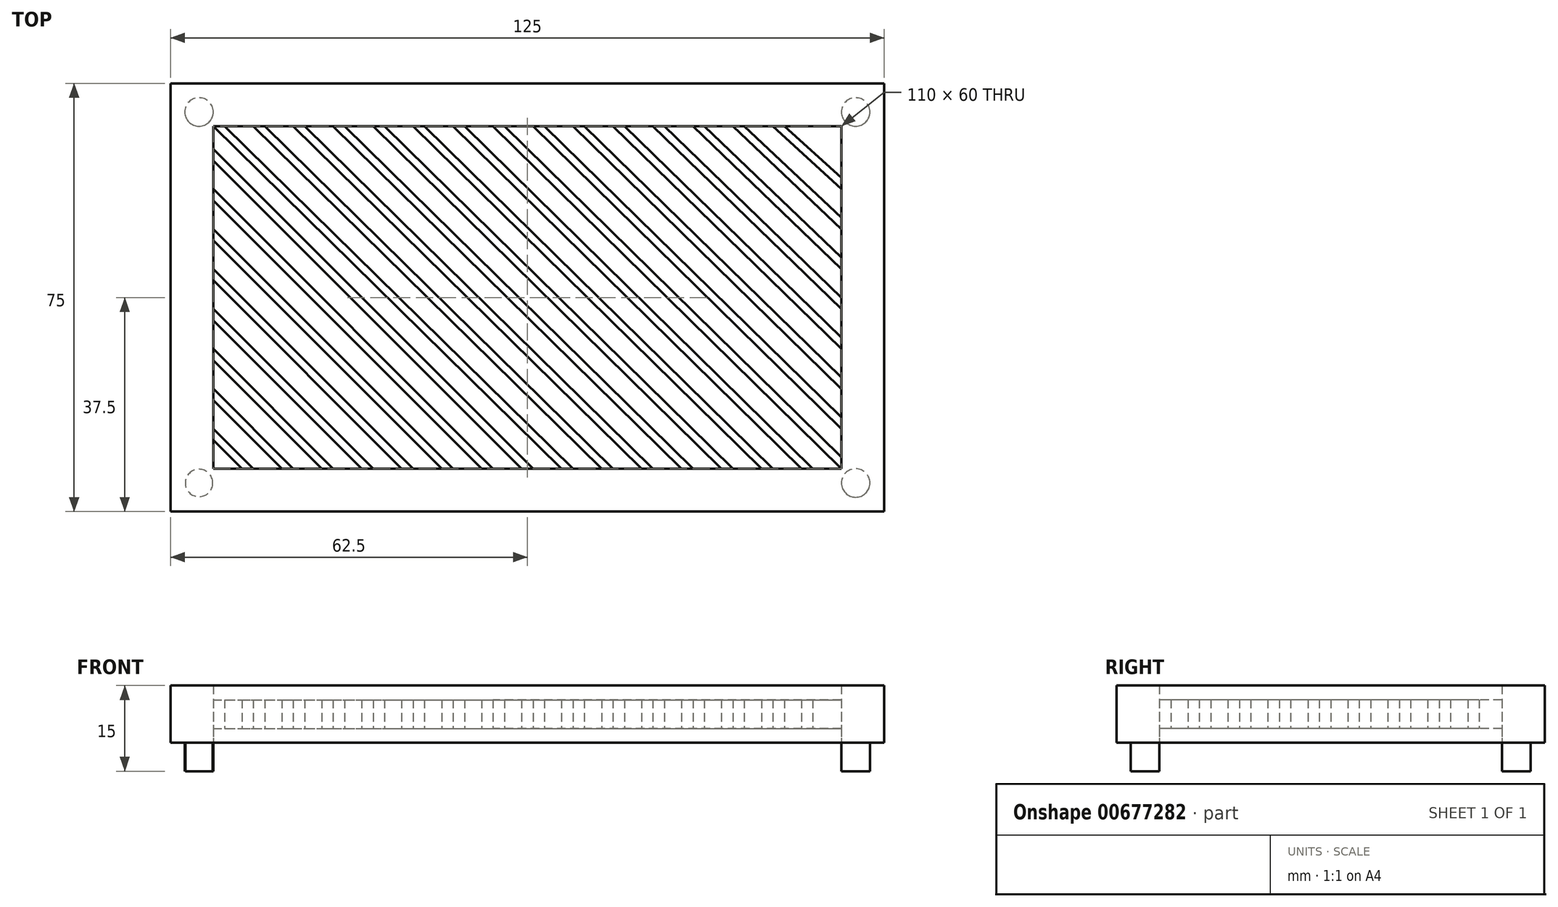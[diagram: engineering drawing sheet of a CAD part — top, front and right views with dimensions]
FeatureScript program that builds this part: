
annotation { "Feature Type Name" : "Feature", "Feature Type Description" : "" }
export const myFeature = defineFeature(function(context is Context, id is Id, definition is map)
    precondition{}
    {
        {
            var Q0;
            Q0=qCreatedBy(makeId("Top.planeOp"),FACE);
            var sketch = newSketch(context, id + "F0", { "sketchPlane" : qUnion([Q0])});
            skLineSegment(sketch, "E0.bottom", {"start": v(-55, 30) * mm, "end": v(55, 30) * mm});
            skLineSegment(sketch, "E0.top", {"start": v(-55, -30) * mm, "end": v(55, -30) * mm});
            skLineSegment(sketch, "E0.left", {"start": v(-55, 30) * mm, "end": v(-55, -30) * mm});
            skLineSegment(sketch, "E0.right", {"start": v(55, 30) * mm, "end": v(55, -30) * mm});
            skPoint(sketch, "E0.middle", {"position": v(0, 0) * mm});
            skLineSegment(sketch, "E1.bottom", {"start": v(-62.5, 37.5) * mm, "end": v(62.5, 37.5) * mm});
            skLineSegment(sketch, "E1.top", {"start": v(-62.5, -37.5) * mm, "end": v(62.5, -37.5) * mm});
            skLineSegment(sketch, "E1.left", {"start": v(-62.5, 37.5) * mm, "end": v(-62.5, -37.5) * mm});
            skLineSegment(sketch, "E1.right", {"start": v(62.5, 37.5) * mm, "end": v(62.5, -37.5) * mm});
            skLineSegment(sketch, "E2", {"start": v(-55, -25) * mm, "end": v(-50, -30) * mm});
            skLineSegment(sketch, "E3", {"start": v(-55, -23) * mm, "end": v(-48, -30) * mm});
            skLineSegment(sketch, "E4", {"start": v(-55, -18) * mm, "end": v(-43, -30) * mm});
            skLineSegment(sketch, "E5", {"start": v(-55, -16) * mm, "end": v(-41, -30) * mm});
            skLineSegment(sketch, "E6", {"start": v(-55, -11) * mm, "end": v(-36, -30) * mm});
            skLineSegment(sketch, "E7", {"start": v(-55, -9) * mm, "end": v(-34, -30) * mm});
            skLineSegment(sketch, "E8", {"start": v(-55, -4) * mm, "end": v(-29, -30) * mm});
            skLineSegment(sketch, "E9", {"start": v(-55, -2) * mm, "end": v(-27, -30) * mm});
            skLineSegment(sketch, "E10", {"start": v(-55, 3) * mm, "end": v(-22, -30) * mm});
            skLineSegment(sketch, "E11", {"start": v(-55, 5) * mm, "end": v(-20, -30) * mm});
            skLineSegment(sketch, "E12", {"start": v(-55, 10) * mm, "end": v(-15, -30) * mm});
            skLineSegment(sketch, "E13", {"start": v(-55, 12) * mm, "end": v(-13, -30) * mm});
            skLineSegment(sketch, "E14", {"start": v(-55, 17) * mm, "end": v(-8, -30) * mm});
            skLineSegment(sketch, "E15", {"start": v(-55, 19) * mm, "end": v(-6, -30) * mm});
            skLineSegment(sketch, "E16", {"start": v(-55, 24) * mm, "end": v(-1, -30) * mm});
            skLineSegment(sketch, "E17", {"start": v(-55, 26) * mm, "end": v(1, -30) * mm});
            skLineSegment(sketch, "E18", {"start": v(-55, 30) * mm, "end": v(6, -30) * mm});
            skLineSegment(sketch, "E19", {"start": v(-53, 30) * mm, "end": v(8, -30) * mm});
            skLineSegment(sketch, "E20", {"start": v(-48, 30) * mm, "end": v(13, -30) * mm});
            skLineSegment(sketch, "E21", {"start": v(-46, 30) * mm, "end": v(15, -30) * mm});
            skLineSegment(sketch, "E22", {"start": v(-41, 30) * mm, "end": v(20, -30) * mm});
            skLineSegment(sketch, "E23", {"start": v(-39, 30) * mm, "end": v(22, -30) * mm});
            skLineSegment(sketch, "E24", {"start": v(-34, 30) * mm, "end": v(27, -30) * mm});
            skLineSegment(sketch, "E25", {"start": v(-32, 30) * mm, "end": v(29, -30) * mm});
            skLineSegment(sketch, "E26", {"start": v(-27, 30) * mm, "end": v(34, -30) * mm});
            skLineSegment(sketch, "E27", {"start": v(-25, 30) * mm, "end": v(36, -30) * mm});
            skLineSegment(sketch, "E28", {"start": v(-20, 30) * mm, "end": v(41, -30) * mm});
            skLineSegment(sketch, "E29", {"start": v(-18, 30) * mm, "end": v(43, -30) * mm});
            skLineSegment(sketch, "E30", {"start": v(-13, 30) * mm, "end": v(48, -30) * mm});
            skLineSegment(sketch, "E31", {"start": v(-11, 30) * mm, "end": v(50, -30) * mm});
            skLineSegment(sketch, "E32", {"start": v(55, -30) * mm, "end": v(-6, 30) * mm});
            skLineSegment(sketch, "E33", {"start": v(1, 30) * mm, "end": v(55, -23) * mm});
            skLineSegment(sketch, "E34", {"start": v(3, 30) * mm, "end": v(55, -21) * mm});
            skLineSegment(sketch, "E35", {"start": v(8, 30) * mm, "end": v(55, -16) * mm});
            skLineSegment(sketch, "E36", {"start": v(10, 30) * mm, "end": v(55, -14) * mm});
            skLineSegment(sketch, "E37", {"start": v(15, 30) * mm, "end": v(55, -9) * mm});
            skLineSegment(sketch, "E38", {"start": v(17, 30) * mm, "end": v(55, -7) * mm});
            skLineSegment(sketch, "E39", {"start": v(22, 30) * mm, "end": v(55, -2) * mm});
            skLineSegment(sketch, "E40", {"start": v(24, 30) * mm, "end": v(55, 0) * mm});
            skLineSegment(sketch, "E41", {"start": v(29, 30) * mm, "end": v(55, 5) * mm});
            skLineSegment(sketch, "E42", {"start": v(31, 30) * mm, "end": v(55, 7) * mm});
            skLineSegment(sketch, "E43", {"start": v(36, 30) * mm, "end": v(55, 12) * mm});
            skLineSegment(sketch, "E44", {"start": v(38, 30) * mm, "end": v(55, 14) * mm});
            skLineSegment(sketch, "E45", {"start": v(43, 30) * mm, "end": v(55, 19) * mm});
            skLineSegment(sketch, "E46", {"start": v(45, 30) * mm, "end": v(55, 21) * mm});
            skLineSegment(sketch, "E47", {"start": v(-4, 30) * mm, "end": v(55, -28) * mm});
            skSolve(sketch);
        }
        {
            var Q0;
            {var subQ9=sQuery(id+"F0.wireOp",EDGE,"E0.bottom");Q0=makeQuery(id+"F0.imprint","IMPRINT",FACE,{"disambiguationData":[TD([[makeQuery(id+"F0.imprint","IMPRINT",EDGE,{"derivedFrom":subQ9}),1.0]])]});}
            extrude(context, id + "F1", {"entities" : qUnion([Q0]), "endBound" : BoundingType.SYMMETRIC, "depth" : 10 * mm, "offsetDistance" : 25 * mm});
        }
        {
            var Q0;
            {var subQ0=sQuery(id+"F0.wireOp",EDGE,"E2");Q0=makeQuery(id+"F0.imprint","IMPRINT",FACE,{"disambiguationData":[TD([[makeQuery(id+"F0.imprint","IMPRINT",EDGE,{"derivedFrom":subQ0}),1.0]])]});}
            var Q1;
            {var subQ0=sQuery(id+"F0.wireOp",EDGE,"E4");Q1=makeQuery(id+"F0.imprint","IMPRINT",FACE,{"disambiguationData":[TD([[makeQuery(id+"F0.imprint","IMPRINT",EDGE,{"derivedFrom":subQ0}),1.0]])]});}
            var Q2;
            {var subQ0=sQuery(id+"F0.wireOp",EDGE,"E6");Q2=makeQuery(id+"F0.imprint","IMPRINT",FACE,{"disambiguationData":[TD([[makeQuery(id+"F0.imprint","IMPRINT",EDGE,{"derivedFrom":subQ0}),1.0]])]});}
            var Q3;
            {var subQ0=sQuery(id+"F0.wireOp",EDGE,"E8");Q3=makeQuery(id+"F0.imprint","IMPRINT",FACE,{"disambiguationData":[TD([[makeQuery(id+"F0.imprint","IMPRINT",EDGE,{"derivedFrom":subQ0}),1.0]])]});}
            var Q4;
            {var subQ0=sQuery(id+"F0.wireOp",EDGE,"E10");Q4=makeQuery(id+"F0.imprint","IMPRINT",FACE,{"disambiguationData":[TD([[makeQuery(id+"F0.imprint","IMPRINT",EDGE,{"derivedFrom":subQ0}),1.0]])]});}
            var Q5;
            {var subQ0=sQuery(id+"F0.wireOp",EDGE,"E12");Q5=makeQuery(id+"F0.imprint","IMPRINT",FACE,{"disambiguationData":[TD([[makeQuery(id+"F0.imprint","IMPRINT",EDGE,{"derivedFrom":subQ0}),1.0]])]});}
            var Q6;
            {var subQ0=sQuery(id+"F0.wireOp",EDGE,"E14");Q6=makeQuery(id+"F0.imprint","IMPRINT",FACE,{"disambiguationData":[TD([[makeQuery(id+"F0.imprint","IMPRINT",EDGE,{"derivedFrom":subQ0}),1.0]])]});}
            var Q7;
            {var subQ0=sQuery(id+"F0.wireOp",EDGE,"E16");Q7=makeQuery(id+"F0.imprint","IMPRINT",FACE,{"disambiguationData":[TD([[makeQuery(id+"F0.imprint","IMPRINT",EDGE,{"derivedFrom":subQ0}),1.0]])]});}
            var Q8;
            {var subQ0=sQuery(id+"F0.wireOp",EDGE,"E18");Q8=makeQuery(id+"F0.imprint","IMPRINT",FACE,{"disambiguationData":[TD([[makeQuery(id+"F0.imprint","IMPRINT",EDGE,{"derivedFrom":subQ0}),1.0]])]});}
            var Q9;
            {var subQ0=sQuery(id+"F0.wireOp",EDGE,"E20");Q9=makeQuery(id+"F0.imprint","IMPRINT",FACE,{"disambiguationData":[TD([[makeQuery(id+"F0.imprint","IMPRINT",EDGE,{"derivedFrom":subQ0}),1.0]])]});}
            var Q10;
            {var subQ0=sQuery(id+"F0.wireOp",EDGE,"E22");Q10=makeQuery(id+"F0.imprint","IMPRINT",FACE,{"disambiguationData":[TD([[makeQuery(id+"F0.imprint","IMPRINT",EDGE,{"derivedFrom":subQ0}),1.0]])]});}
            var Q11;
            {var subQ0=sQuery(id+"F0.wireOp",EDGE,"E24");Q11=makeQuery(id+"F0.imprint","IMPRINT",FACE,{"disambiguationData":[TD([[makeQuery(id+"F0.imprint","IMPRINT",EDGE,{"derivedFrom":subQ0}),1.0]])]});}
            var Q12;
            {var subQ0=sQuery(id+"F0.wireOp",EDGE,"E26");Q12=makeQuery(id+"F0.imprint","IMPRINT",FACE,{"disambiguationData":[TD([[makeQuery(id+"F0.imprint","IMPRINT",EDGE,{"derivedFrom":subQ0}),1.0]])]});}
            var Q13;
            {var subQ0=sQuery(id+"F0.wireOp",EDGE,"E28");Q13=makeQuery(id+"F0.imprint","IMPRINT",FACE,{"disambiguationData":[TD([[makeQuery(id+"F0.imprint","IMPRINT",EDGE,{"derivedFrom":subQ0}),1.0]])]});}
            var Q14;
            {var subQ0=sQuery(id+"F0.wireOp",EDGE,"E30");Q14=makeQuery(id+"F0.imprint","IMPRINT",FACE,{"disambiguationData":[TD([[makeQuery(id+"F0.imprint","IMPRINT",EDGE,{"derivedFrom":subQ0}),1.0]])]});}
            var Q15;
            {var subQ0=sQuery(id+"F0.wireOp",EDGE,"E33");Q15=makeQuery(id+"F0.imprint","IMPRINT",FACE,{"disambiguationData":[TD([[makeQuery(id+"F0.imprint","IMPRINT",EDGE,{"derivedFrom":subQ0}),1.0]])]});}
            var Q16;
            {var subQ0=sQuery(id+"F0.wireOp",EDGE,"E35");Q16=makeQuery(id+"F0.imprint","IMPRINT",FACE,{"disambiguationData":[TD([[makeQuery(id+"F0.imprint","IMPRINT",EDGE,{"derivedFrom":subQ0}),1.0]])]});}
            var Q17;
            {var subQ0=sQuery(id+"F0.wireOp",EDGE,"E45");Q17=makeQuery(id+"F0.imprint","IMPRINT",FACE,{"disambiguationData":[TD([[makeQuery(id+"F0.imprint","IMPRINT",EDGE,{"derivedFrom":subQ0}),1.0]])]});}
            var Q18;
            {var subQ0=sQuery(id+"F0.wireOp",EDGE,"E43");Q18=makeQuery(id+"F0.imprint","IMPRINT",FACE,{"disambiguationData":[TD([[makeQuery(id+"F0.imprint","IMPRINT",EDGE,{"derivedFrom":subQ0}),1.0]])]});}
            var Q19;
            {var subQ0=sQuery(id+"F0.wireOp",EDGE,"E41");Q19=makeQuery(id+"F0.imprint","IMPRINT",FACE,{"disambiguationData":[TD([[makeQuery(id+"F0.imprint","IMPRINT",EDGE,{"derivedFrom":subQ0}),1.0]])]});}
            var Q20;
            {var subQ0=sQuery(id+"F0.wireOp",EDGE,"E39");Q20=makeQuery(id+"F0.imprint","IMPRINT",FACE,{"disambiguationData":[TD([[makeQuery(id+"F0.imprint","IMPRINT",EDGE,{"derivedFrom":subQ0}),1.0]])]});}
            var Q21;
            {var subQ0=sQuery(id+"F0.wireOp",EDGE,"E37");Q21=makeQuery(id+"F0.imprint","IMPRINT",FACE,{"disambiguationData":[TD([[makeQuery(id+"F0.imprint","IMPRINT",EDGE,{"derivedFrom":subQ0}),1.0]])]});}
            var Q22;
            {var subQ0=sQuery(id+"F0.wireOp",EDGE,"E32");Q22=makeQuery(id+"F0.imprint","IMPRINT",FACE,{"disambiguationData":[TD([[makeQuery(id+"F0.imprint","IMPRINT",EDGE,{"derivedFrom":subQ0}),-1.0]])]});}
            extrude(context, id + "F2", {"entities" : qUnion([Q0, Q1, Q2, Q3, Q4, Q5, Q6, Q7, Q8, Q9, Q10, Q11, Q12, Q13, Q14, Q15, Q16, Q17, Q18, Q19, Q20, Q21, Q22]), "operationType" : NewBodyOperationType.ADD, "endBound" : BoundingType.SYMMETRIC, "depth" : 5 * mm, "offsetDistance" : 25 * mm});
        }
        {
            var Q0;
            Q0=makeQuery(id+"F1.opExtrude","CAP_FACE",FACE,{"disambiguationData":[OSD([sQuery(id+"F0.wireOp",EDGE,"E0.bottom"),sQuery(id+"F0.wireOp",EDGE,"E0.top"),sQuery(id+"F0.wireOp",EDGE,"E0.left"),sQuery(id+"F0.wireOp",EDGE,"E0.right"),sQuery(id+"F0.wireOp",EDGE,"E1.bottom"),sQuery(id+"F0.wireOp",EDGE,"E1.top"),sQuery(id+"F0.wireOp",EDGE,"E1.left"),sQuery(id+"F0.wireOp",EDGE,"E1.right")])],"isStart":true});
            var sketch = newSketch(context, id + "F3", { "sketchPlane" : qUnion([Q0])});
            skCircle(sketch, "E48", {"center": v(-57.5, 32.5) * mm, "radius": 2.4 * mm});
            skCircle(sketch, "E49", {"center": v(57.5, 32.5) * mm, "radius": 2.5 * mm});
            skCircle(sketch, "E50", {"center": v(57.5, -32.5) * mm, "radius": 2.5 * mm});
            skCircle(sketch, "E51", {"center": v(-57.5, -32.5) * mm, "radius": 2.5 * mm});
            skSolve(sketch);
        }
        {
            var Q0;
            Q0 = qSketchRegion(id + "F3", true);
            extrude(context, id + "F4", {"entities" : qUnion([Q0]), "operationType" : NewBodyOperationType.ADD, "depth" : 5 * mm, "offsetDistance" : 25 * mm});
        }
    });
